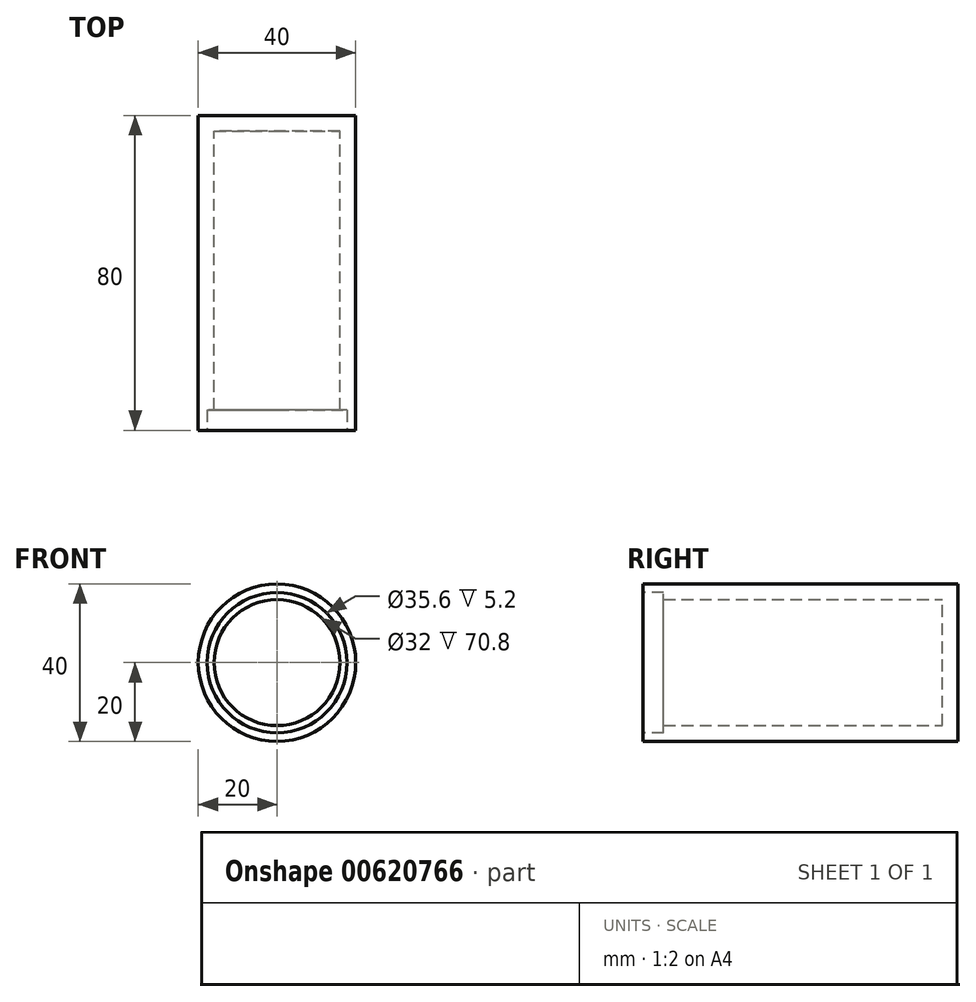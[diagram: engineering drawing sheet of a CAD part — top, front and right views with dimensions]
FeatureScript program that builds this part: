
annotation { "Feature Type Name" : "Feature", "Feature Type Description" : "" }
export const myFeature = defineFeature(function(context is Context, id is Id, definition is map)
    precondition{}
    {
        {
            var Q0;
            Q0=qCreatedBy(makeId("Front.planeOp"),FACE);
            var sketch = newSketch(context, id + "F0", { "sketchPlane" : qUnion([Q0])});
            skCircle(sketch, "E0", {"center": v(0, 0) * mm, "radius": 20 * mm});
            skSolve(sketch);
        }
        {
            var Q0;
            Q0=makeQuery(id+"F0.imprint","IMPRINT",FACE,{"disambiguationData":[TD([[makeQuery(id+"F0.imprint","IMPRINT",EDGE,{"derivedFrom":sQuery(id+"F0.wireOp",EDGE,"E0")}),1.0]])]});
            extrude(context, id + "F1", {"entities" : qUnion([Q0]), "depth" : 80 * mm, "offsetDistance" : 25 * mm});
        }
        {
            var Q0;
            Q0=makeQuery(id+"F1.opExtrude","CAP_FACE",FACE,{"disambiguationData":[OSD([sQuery(id+"F0.wireOp",EDGE,"E0")])],"isStart":false});
            shell(context, id + "F2", {"entities" : qUnion([Q0]), "thickness" : 4 * mm});
        }
        {
            var Q0;
            Q0=makeQuery(id+"F1.opExtrude","CAP_FACE",FACE,{"disambiguationData":[OSD([sQuery(id+"F0.wireOp",EDGE,"E0")])],"isStart":false});
            var sketch = newSketch(context, id + "F3", { "sketchPlane" : qUnion([Q0])});
            skCircle(sketch, "E1", {"center": v(0, 0) * mm, "radius": 17.8 * mm});
            skSolve(sketch);
        }
        {
            var Q0;
            Q0 = qSketchRegion(id + "F3", true);
            extrude(context, id + "F4", {"entities" : qUnion([Q0]), "operationType" : NewBodyOperationType.REMOVE, "oppositeDirection" : true, "depth" : 5.2 * mm, "offsetDistance" : 25 * mm});
        }
    });
